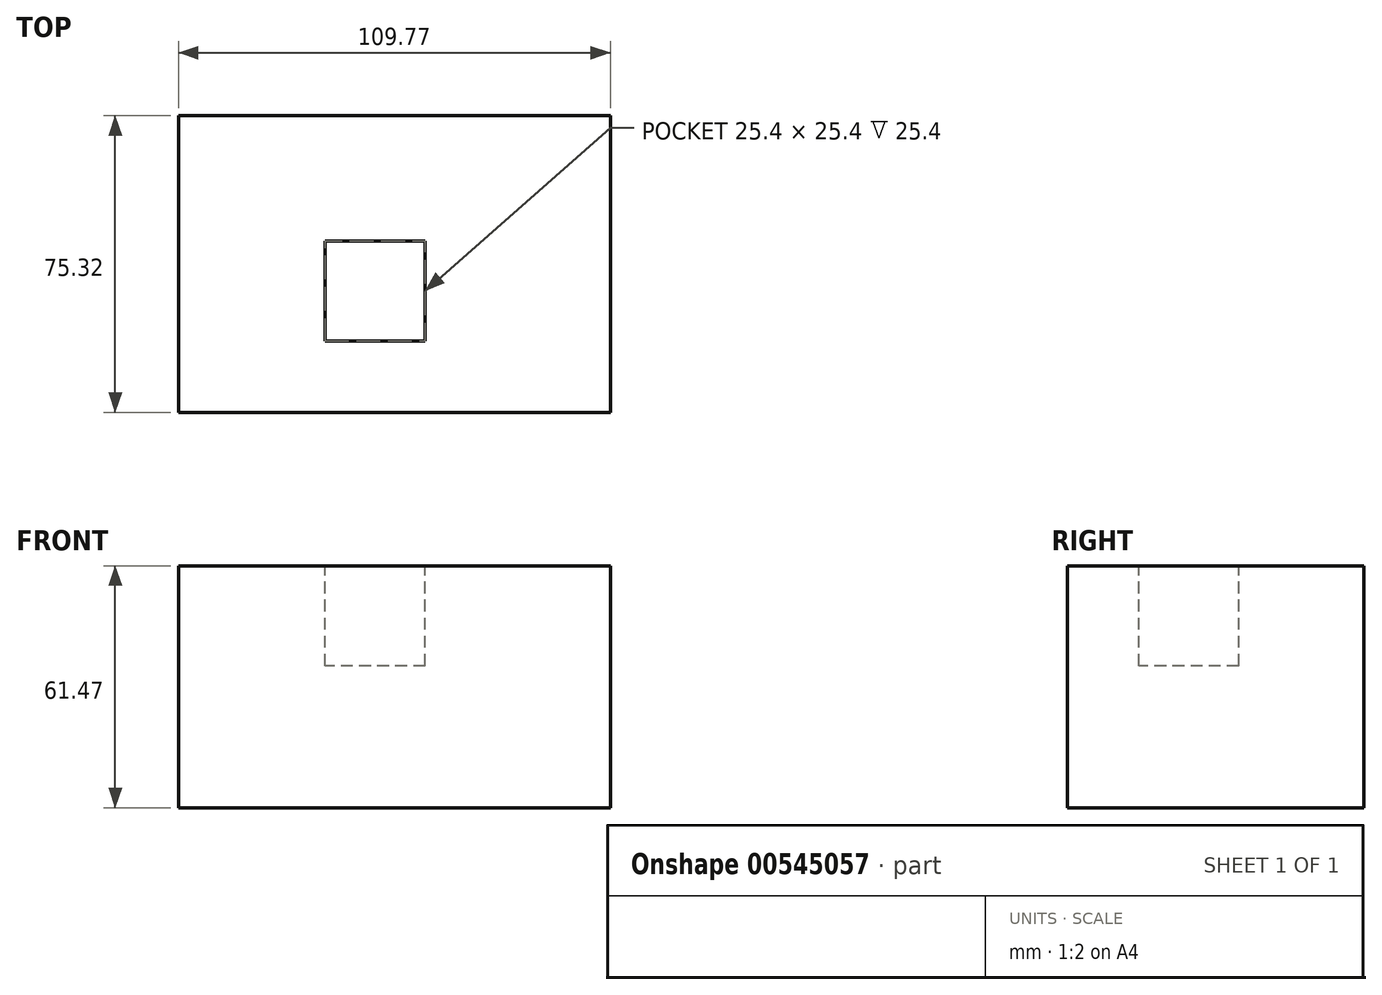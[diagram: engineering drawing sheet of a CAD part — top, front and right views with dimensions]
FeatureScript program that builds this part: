
annotation { "Feature Type Name" : "Feature", "Feature Type Description" : "" }
export const myFeature = defineFeature(function(context is Context, id is Id, definition is map)
    precondition{}
    {
        {
            var Q0;
            Q0=qCreatedBy(makeId("Top.planeOp"),FACE);
            var sketch = newSketch(context, id + "F0", { "sketchPlane" : qUnion([Q0])});
            skLineSegment(sketch, "E0.bottom", {"start": v(-49.05, 33.13) * mm, "end": v(60.72, 33.13) * mm});
            skLineSegment(sketch, "E0.top", {"start": v(-49.05, -42.2) * mm, "end": v(60.72, -42.2) * mm});
            skLineSegment(sketch, "E0.left", {"start": v(-49.05, 33.13) * mm, "end": v(-49.05, -42.2) * mm});
            skLineSegment(sketch, "E0.right", {"start": v(60.72, 33.13) * mm, "end": v(60.72, -42.2) * mm});
            skSolve(sketch);
        }
        {
            var Q0;
            Q0=makeQuery(id+"F0.imprint","IMPRINT",FACE,{"disambiguationData":[TD([[makeQuery(id+"F0.imprint","IMPRINT",EDGE,{"derivedFrom":sQuery(id+"F0.wireOp",EDGE,"E0.bottom")}),-1.0]])]});
            extrude(context, id + "F1", {"entities" : qUnion([Q0]), "depth" : 61.47 * mm, "offsetDistance" : 25.4 * mm});
        }
        {
            var Q0;
            Q0=makeQuery(id+"F1.opExtrude","CAP_FACE",FACE,{"disambiguationData":[OSD([sQuery(id+"F0.wireOp",EDGE,"E0.bottom"),sQuery(id+"F0.wireOp",EDGE,"E0.top"),sQuery(id+"F0.wireOp",EDGE,"E0.left"),sQuery(id+"F0.wireOp",EDGE,"E0.right")])],"isStart":false});
            var sketch = newSketch(context, id + "F2", { "sketchPlane" : qUnion([Q0])});
            skLineSegment(sketch, "E1.0.0", {"start": v(-49.05, 33.13) * mm, "end": v(-49.05, -42.2) * mm});
            skLineSegment(sketch, "E1.0.1", {"start": v(-49.05, -42.2) * mm, "end": v(60.72, -42.2) * mm});
            skLineSegment(sketch, "E1.0.2", {"start": v(60.72, -42.2) * mm, "end": v(60.72, 33.13) * mm});
            skLineSegment(sketch, "E1.0.3", {"start": v(60.72, 33.13) * mm, "end": v(-49.05, 33.13) * mm});
            skPoint(sketch, "E2", {"position": v(60.72, -11.82) * mm});
            skLineSegment(sketch, "E3.bottom", {"start": v(13.66, 1.34) * mm, "end": v(-11.74, 1.34) * mm});
            skLineSegment(sketch, "E3.top", {"start": v(13.66, -24.06) * mm, "end": v(-11.74, -24.06) * mm});
            skLineSegment(sketch, "E3.left", {"start": v(13.66, 1.34) * mm, "end": v(13.66, -24.06) * mm});
            skLineSegment(sketch, "E3.right", {"start": v(-11.74, 1.34) * mm, "end": v(-11.74, -24.06) * mm});
            skPoint(sketch, "E3.middle", {"position": v(0.96, -11.36) * mm});
            skSolve(sketch);
        }
        {
            var Q0;
            Q0=makeQuery(id+"F2.imprint","IMPRINT",FACE,{"disambiguationData":[TD([[makeQuery(id+"F2.imprint","IMPRINT",EDGE,{"derivedFrom":sQuery(id+"F2.wireOp",EDGE,"E3.bottom")}),1.0]])]});
            extrude(context, id + "F3", {"entities" : qUnion([Q0]), "operationType" : NewBodyOperationType.REMOVE, "oppositeDirection" : true, "depth" : 25.4 * mm, "offsetDistance" : 25.4 * mm});
        }
    });
